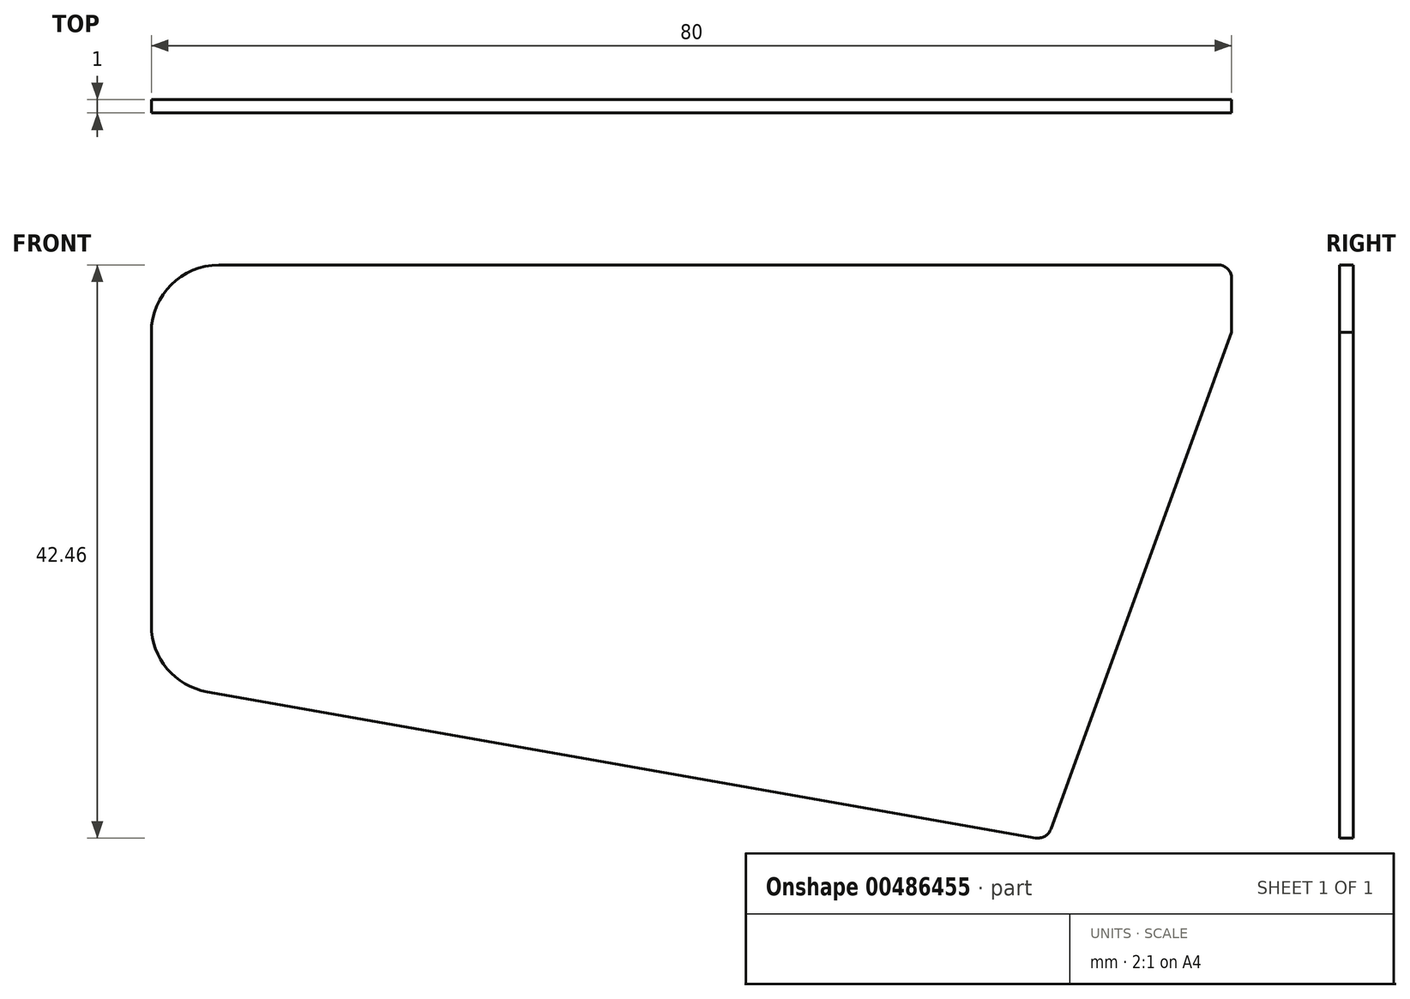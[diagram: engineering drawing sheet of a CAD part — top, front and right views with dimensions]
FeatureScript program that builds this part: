
annotation { "Feature Type Name" : "Feature", "Feature Type Description" : "" }
export const myFeature = defineFeature(function(context is Context, id is Id, definition is map)
    precondition{}
    {
        {
            var Q0;
            Q0=qCreatedBy(makeId("Front.planeOp"),FACE);
            var sketch = newSketch(context, id + "F0", { "sketchPlane" : qUnion([Q0])});
            skLineSegment(sketch, "E0", {"start": v(0, 0) * mm, "end": v(80, 0) * mm});
            skLineSegment(sketch, "E1", {"start": v(80, 0) * mm, "end": v(80, 4) * mm});
            skLineSegment(sketch, "E2", {"start": v(0, 0) * mm, "end": v(0, 0) * mm});
            skLineSegment(sketch, "E3", {"start": v(5, 5) * mm, "end": v(79, 5) * mm});
            skLineSegment(sketch, "E4", {"start": v(80, 0) * mm, "end": v(66.6, -36.8) * mm});
            skPoint(sketch, "E5.visualSharp", {"position": v(0, 5) * mm});
            skArc(sketch, "E5.filletArc", {"start": v(5, 5) * mm, "mid": v(1.46, 3.54) * mm, "end": v(0, 0) * mm});
            skLineSegment(sketch, "E6", {"start": v(65.5, -37.44) * mm, "end": v(4.13, -26.62) * mm});
            skLineSegment(sketch, "E7", {"start": v(0, 0) * mm, "end": v(0, -21.7) * mm});
            skPoint(sketch, "E8.visualSharp", {"position": v(80, 5) * mm});
            skArc(sketch, "E8.filletArc", {"start": v(80, 4) * mm, "mid": v(79.7, 4.7) * mm, "end": v(79, 5) * mm});
            skPoint(sketch, "E9.visualSharp", {"position": v(66.32, -37.59) * mm});
            skArc(sketch, "E9.filletArc", {"start": v(65.5, -37.44) * mm, "mid": v(66.17, -37.32) * mm, "end": v(66.6, -36.8) * mm});
            skPoint(sketch, "E10.visualSharp", {"position": v(0, -25.9) * mm});
            skArc(sketch, "E10.filletArc", {"start": v(0, -21.7) * mm, "mid": v(1.17, -24.91) * mm, "end": v(4.13, -26.62) * mm});
            skSolve(sketch);
        }
        {
            var Q0;
            Q0=makeQuery(id+"F0.imprint","IMPRINT",FACE,{"disambiguationData":[TD([[makeQuery(id+"F0.imprint","IMPRINT",EDGE,{"derivedFrom":sQuery(id+"F0.wireOp",EDGE,"E0")}),1.0]])]});
            var Q1;
            Q1=makeQuery(id+"F0.imprint","IMPRINT",FACE,{"disambiguationData":[TD([[makeQuery(id+"F0.imprint","IMPRINT",EDGE,{"derivedFrom":sQuery(id+"F0.wireOp",EDGE,"E0")}),-1.0]])]});
            extrude(context, id + "F1", {"entities" : qUnion([Q0, Q1]), "endBound" : BoundingType.SYMMETRIC, "oppositeDirection" : true, "depth" : 1 * mm, "offsetDistance" : 25 * mm});
        }
    });
